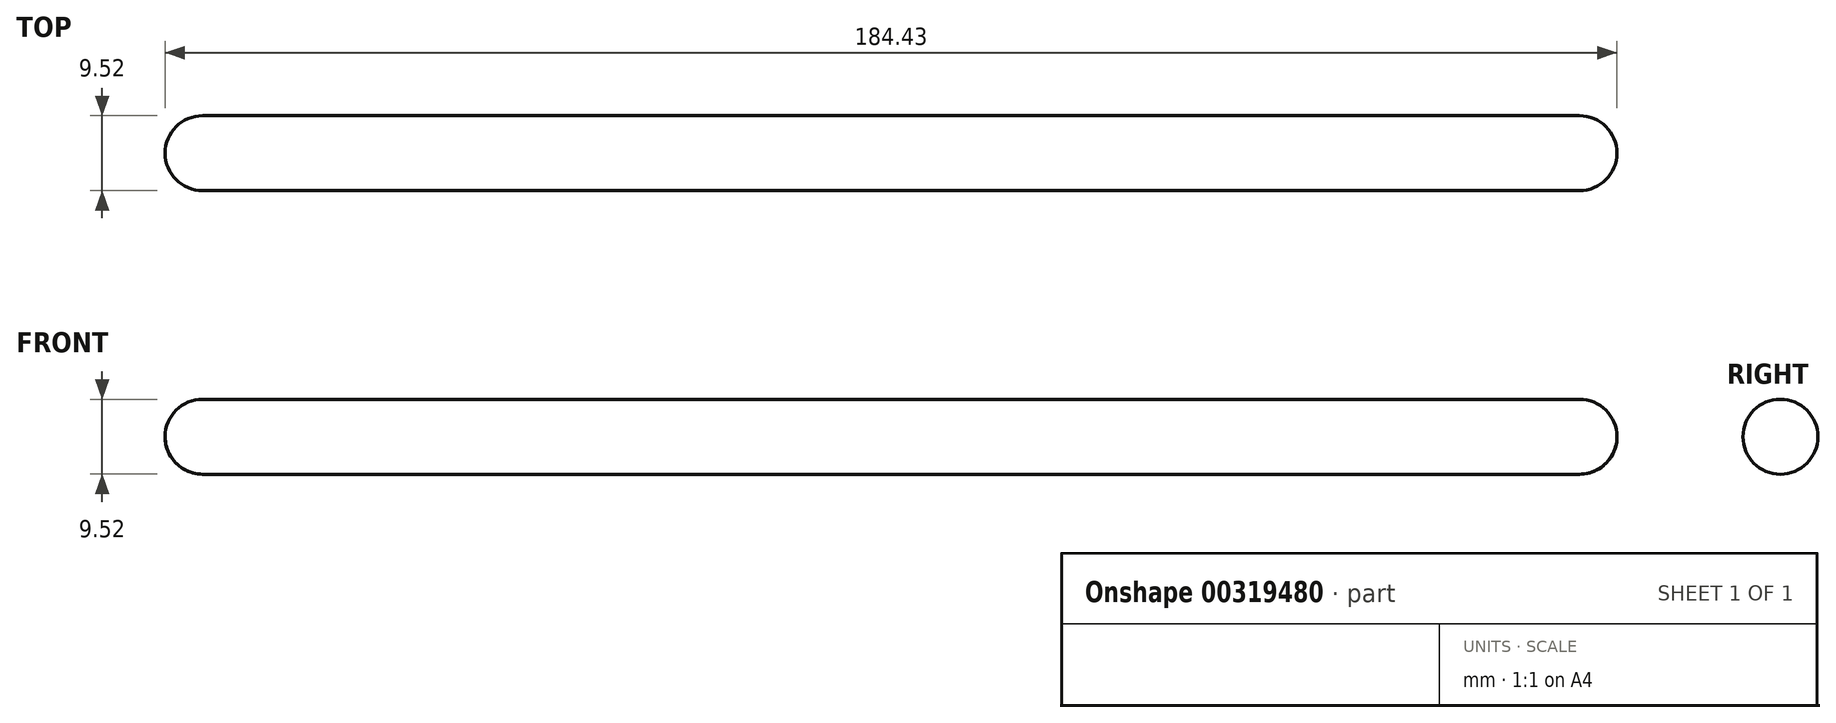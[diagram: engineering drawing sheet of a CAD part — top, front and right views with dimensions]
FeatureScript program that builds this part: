
annotation { "Feature Type Name" : "Feature", "Feature Type Description" : "" }
export const myFeature = defineFeature(function(context is Context, id is Id, definition is map)
    precondition{}
    {
        {
            var Q0;
            Q0=qCreatedBy(makeId("Front.planeOp"),FACE);
            var sketch = newSketch(context, id + "F0", { "sketchPlane" : qUnion([Q0])});
            skLineSegment(sketch, "E0", {"start": v(0, 0) * mm, "end": v(184.43, 0) * mm});
            skPoint(sketch, "E1.startSnap0", {"position": v(92.21, 0) * mm});
            skLineSegment(sketch, "E2", {"start": v(184.43, -4.76) * mm, "end": v(0, -4.76) * mm});
            skLineSegment(sketch, "E3", {"start": v(92.21, 28.28) * mm, "end": v(92.21, -24.43) * mm, "construction": true});
            skLineSegment(sketch, "E4.MirrorCS", {"start": v(92.21, 0) * mm, "end": v(0, 0) * mm});
            skPoint(sketch, "E5.orphan", {"position": v(184.43, -4.76) * mm});
            skPoint(sketch, "E6.end.orphan", {"position": v(0, -4.76) * mm});
            skLineSegment(sketch, "E7", {"start": v(184.43, 0) * mm, "end": v(184.43, -4.76) * mm});
            skPoint(sketch, "E8.orphan", {"position": v(184.43, 0) * mm});
            skArc(sketch, "E9", {"start": v(179.67, -4.76) * mm, "mid": v(183.03, -3.37) * mm, "end": v(184.43, 0) * mm});
            skLineSegment(sketch, "E10", {"start": v(179.67, 0) * mm, "end": v(184.43, 0) * mm});
            skArc(sketch, "E11.MirrorC", {"start": v(4.76, -4.76) * mm, "mid": v(1.4, -3.37) * mm, "end": v(0, 0) * mm});
            skSolve(sketch);
        }
        {
            var Q0;
            {var subQ0=sQuery(id+"F0.wireOp",EDGE,"5uYhxpgL-SeU8-sKq1-xQx1-tVbQcHsfw73k");Q0=makeQuery(id+"F0.imprint","IMPRINT",FACE,{"disambiguationData":[TD([[makeQuery(id+"F0.imprint","IMPRINT",EDGE,{"derivedFrom":subQ0}),1.0]])]});}
            var Q1;
            {var subQ0=sQuery(id+"F0.wireOp",EDGE,"401f2482-f0f0-4185-922d-bb9b8ef0ba5a0.MirrorCS");Q1=makeQuery(id+"F0.imprint","IMPRINT",FACE,{"disambiguationData":[TD([[makeQuery(id+"F0.imprint","IMPRINT",EDGE,{"derivedFrom":subQ0}),-1.0]])]});}
            var Q2;
            Q2=makeQuery(id+"F0.imprint","IMPRINT",FACE,{"disambiguationData":[TD([[makeQuery(id+"F0.imprint","IMPRINT",EDGE,{"derivedFrom":sQuery(id+"F0.wireOp",EDGE,"E0")}),-1.0]])]});
            var Q3;
            Q3=sQuery(id+"F0.wireOp",EDGE,"E4.MirrorCS");
            revolve(context, id + "F1", {"entities" : qUnion([Q0, Q1, Q2]), "axis" : qUnion([Q3]), "revolveType" : RevolveType.FULL});
        }
    });
